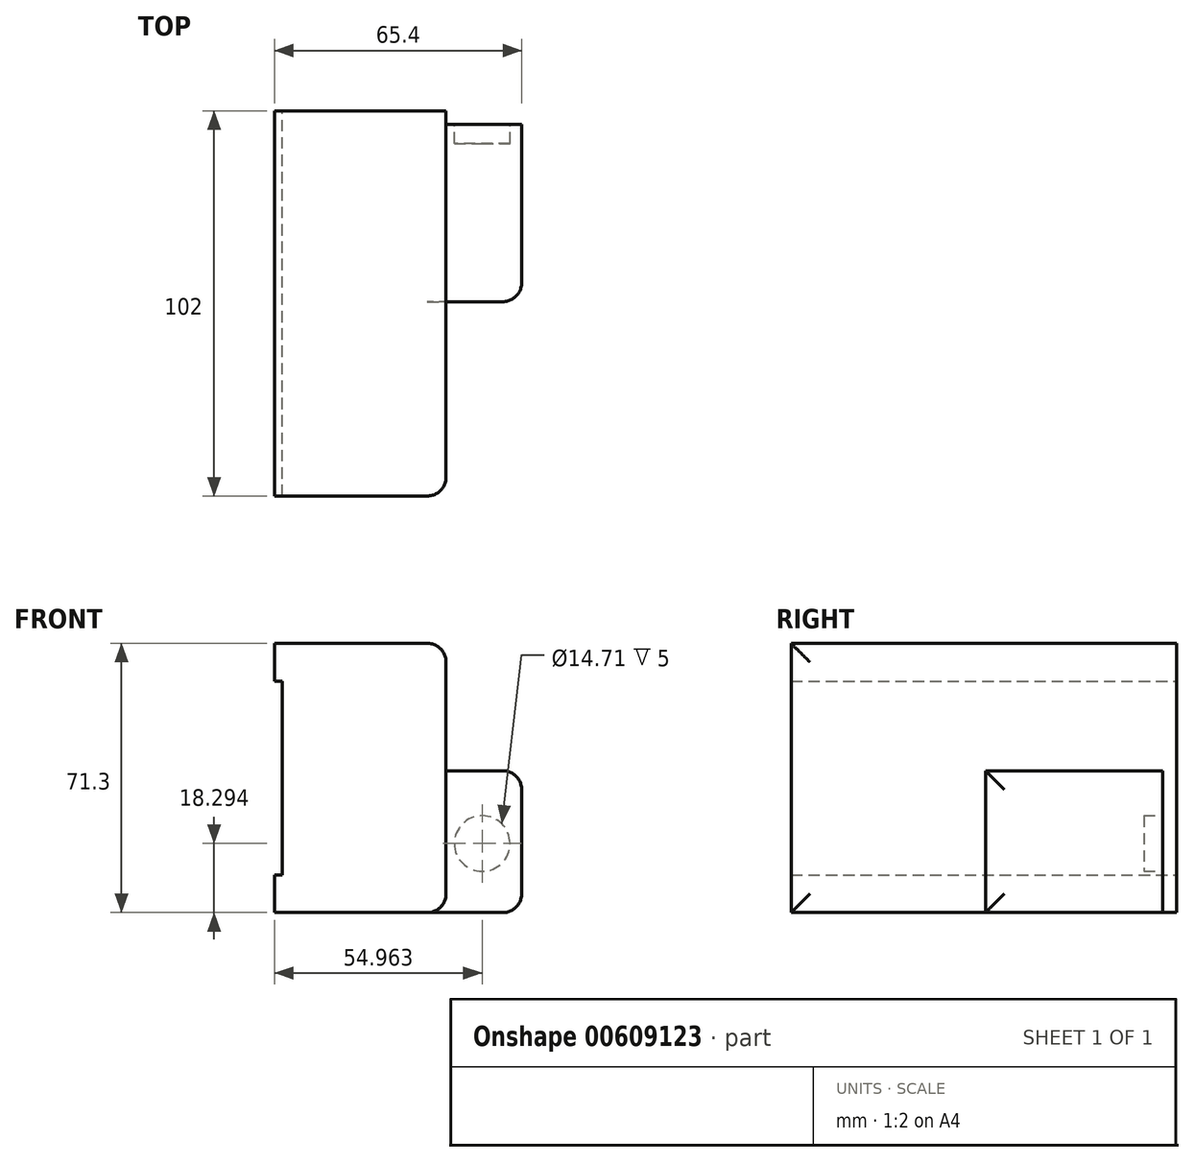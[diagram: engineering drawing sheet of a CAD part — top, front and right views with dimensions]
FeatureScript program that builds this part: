
annotation { "Feature Type Name" : "Feature", "Feature Type Description" : "" }
export const myFeature = defineFeature(function(context is Context, id is Id, definition is map)
    precondition{}
    {
        {
            var Q0;
            Q0=qCreatedBy(makeId("Right.planeOp"),FACE);
            var sketch = newSketch(context, id + "F0", { "sketchPlane" : qUnion([Q0])});
            skLineSegment(sketch, "E0.bottom", {"start": v(51, 27.73) * mm, "end": v(-51, 27.73) * mm});
            skLineSegment(sketch, "E0.top", {"start": v(51, -43.57) * mm, "end": v(-51, -43.57) * mm});
            skLineSegment(sketch, "E0.left", {"start": v(51, 27.73) * mm, "end": v(51, -43.57) * mm});
            skLineSegment(sketch, "E0.right", {"start": v(-51, 27.73) * mm, "end": v(-51, -43.57) * mm});
            skPoint(sketch, "E0.middle", {"position": v(0, -7.92) * mm});
            skSolve(sketch);
        }
        {
            var Q0;
            Q0=makeQuery(id+"F0.imprint","IMPRINT",FACE,{"disambiguationData":[TD([[makeQuery(id+"F0.imprint","IMPRINT",EDGE,{"derivedFrom":sQuery(id+"F0.wireOp",EDGE,"E0.bottom")}),1.0]])]});
            extrude(context, id + "F1", {"entities" : qUnion([Q0]), "depth" : 20 * mm, "offsetDistance" : 25.4 * mm, "hasSecondDirection" : true, "secondDirectionOppositeDirection" : true, "secondDirectionDepth" : 25.4 * mm});
        }
        {
            var Q0;
            Q0=makeQuery(id+"F1.opExtrude","CAP_FACE",FACE,{"disambiguationData":[OSD([sQuery(id+"F0.wireOp",EDGE,"E0.bottom"),sQuery(id+"F0.wireOp",EDGE,"E0.top"),sQuery(id+"F0.wireOp",EDGE,"E0.left"),sQuery(id+"F0.wireOp",EDGE,"E0.right")])],"isStart":false});
            var sketch = newSketch(context, id + "F2", { "sketchPlane" : qUnion([Q0])});
            skLineSegment(sketch, "E1.bottom", {"start": v(47.36, -43.57) * mm, "end": v(0.46, -43.57) * mm});
            skLineSegment(sketch, "E1.top", {"start": v(47.36, -6) * mm, "end": v(0.46, -6) * mm});
            skLineSegment(sketch, "E1.left", {"start": v(47.36, -43.57) * mm, "end": v(47.36, -6) * mm});
            skLineSegment(sketch, "E1.right", {"start": v(0.46, -43.57) * mm, "end": v(0.46, -6) * mm});
            skPoint(sketch, "E1.middle", {"position": v(23.9, -24.79) * mm});
            skSolve(sketch);
        }
        {
            var Q0;
            Q0=makeQuery(id+"F2.imprint","IMPRINT",FACE,{"disambiguationData":[TD([[makeQuery(id+"F2.imprint","IMPRINT",EDGE,{"derivedFrom":sQuery(id+"F2.wireOp",EDGE,"E1.bottom")}),-1.0]])]});
            extrude(context, id + "F3", {"entities" : qUnion([Q0]), "operationType" : NewBodyOperationType.ADD, "depth" : 20 * mm, "offsetDistance" : 25.4 * mm});
        }
        {
            var Q0;
            Q0=makeQuery(id+"F3.opExtrude","SWEPT_FACE",FACE,{"disambiguationData":[OSD([sQuery(id+"F2.wireOp",EDGE,"E1.left")])]});
            var sketch = newSketch(context, id + "F4", { "sketchPlane" : qUnion([Q0])});
            skCircle(sketch, "E2", {"center": v(-29.56, -25.28) * mm, "radius": 7.36 * mm});
            skSolve(sketch);
        }
        {
            var Q0;
            Q0 = qSketchRegion(id + "F4", true);
            var Q1;
            Q1=makeQuery(id+"F4.imprint","IMPRINT",FACE,{"disambiguationData":[TD([[makeQuery(id+"F4.imprint","IMPRINT",EDGE,{"derivedFrom":sQuery(id+"F4.wireOp",EDGE,"E2")}),1.0]])]});
            extrude(context, id + "F5", {"entities" : qUnion([Q0, Q1]), "operationType" : NewBodyOperationType.REMOVE, "oppositeDirection" : true, "depth" : 5 * mm, "offsetDistance" : 25.4 * mm});
        }
        {
            var Q0;
            Q0=makeQuery(id+"F1.opExtrude","CAP_EDGE",EDGE,{"disambiguationData":[OSD([sQuery(id+"F0.wireOp",EDGE,"E0.bottom")])],"isStart":false});
            var Q1;
            Q1=makeQuery(id+"F1.opExtrude","CAP_EDGE",EDGE,{"disambiguationData":[OSD([sQuery(id+"F0.wireOp",EDGE,"E0.right")])],"isStart":false});
            var Q2;
            {var subQ0=sQuery(id+"F0.wireOp",EDGE,"E0.right");var subQ1=sQuery(id+"F0.wireOp",EDGE,"E0.top");Q2=makeQuery(id+"F3.boolean.opBoolean","SPLIT",EDGE,{"disambiguationData":[TD([makeQuery(id+"F1.opExtrude","SWEPT_FACE",FACE,{"disambiguationData":[OSD([subQ0])]})])],"derivedFrom":makeQuery(id+"F1.opExtrude","CAP_EDGE",EDGE,{"disambiguationData":[OSD([subQ1])],"isStart":false})});}
            var Q3;
            Q3=makeQuery(id+"F3.opExtrude","CAP_EDGE",EDGE,{"disambiguationData":[OSD([sQuery(id+"F2.wireOp",EDGE,"E1.bottom")])],"isStart":false});
            var Q4;
            Q4=makeQuery(id+"F3.opExtrude","CAP_EDGE",EDGE,{"disambiguationData":[OSD([sQuery(id+"F2.wireOp",EDGE,"E1.top")])],"isStart":false});
            var Q5;
            Q5=makeQuery(id+"F3.opExtrude","CAP_EDGE",EDGE,{"disambiguationData":[OSD([sQuery(id+"F2.wireOp",EDGE,"E1.right")])],"isStart":false});
            fillet(context, id + "F6", {"entities" : qUnion([Q0, Q1, Q2, Q3, Q4, Q5]), "radius" : 5 * mm, "tangentPropagation" : true, "allowEdgeOverflow" : false});
        }
        {
            var Q0;
            Q0=makeQuery(id+"F1.opExtrude","CAP_FACE",FACE,{"disambiguationData":[OSD([sQuery(id+"F0.wireOp",EDGE,"E0.bottom"),sQuery(id+"F0.wireOp",EDGE,"E0.top"),sQuery(id+"F0.wireOp",EDGE,"E0.left"),sQuery(id+"F0.wireOp",EDGE,"E0.right")])],"isStart":true});
            var sketch = newSketch(context, id + "F7", { "sketchPlane" : qUnion([Q0])});
            skLineSegment(sketch, "E3.bottom", {"start": v(115.1, -33.57) * mm, "end": v(-84.9, -33.57) * mm});
            skLineSegment(sketch, "E3.top", {"start": v(115.1, 17.73) * mm, "end": v(-84.9, 17.73) * mm});
            skLineSegment(sketch, "E3.left", {"start": v(115.1, -33.57) * mm, "end": v(115.1, 17.73) * mm});
            skLineSegment(sketch, "E3.right", {"start": v(-84.9, -33.57) * mm, "end": v(-84.9, 17.73) * mm});
            skSolve(sketch);
        }
        {
            var Q0;
            Q0 = qSketchRegion(id + "F7", true);
            extrude(context, id + "F8", {"entities" : qUnion([Q0]), "operationType" : NewBodyOperationType.REMOVE, "oppositeDirection" : true, "depth" : 2 * mm, "offsetDistance" : 25 * mm});
        }
    });
